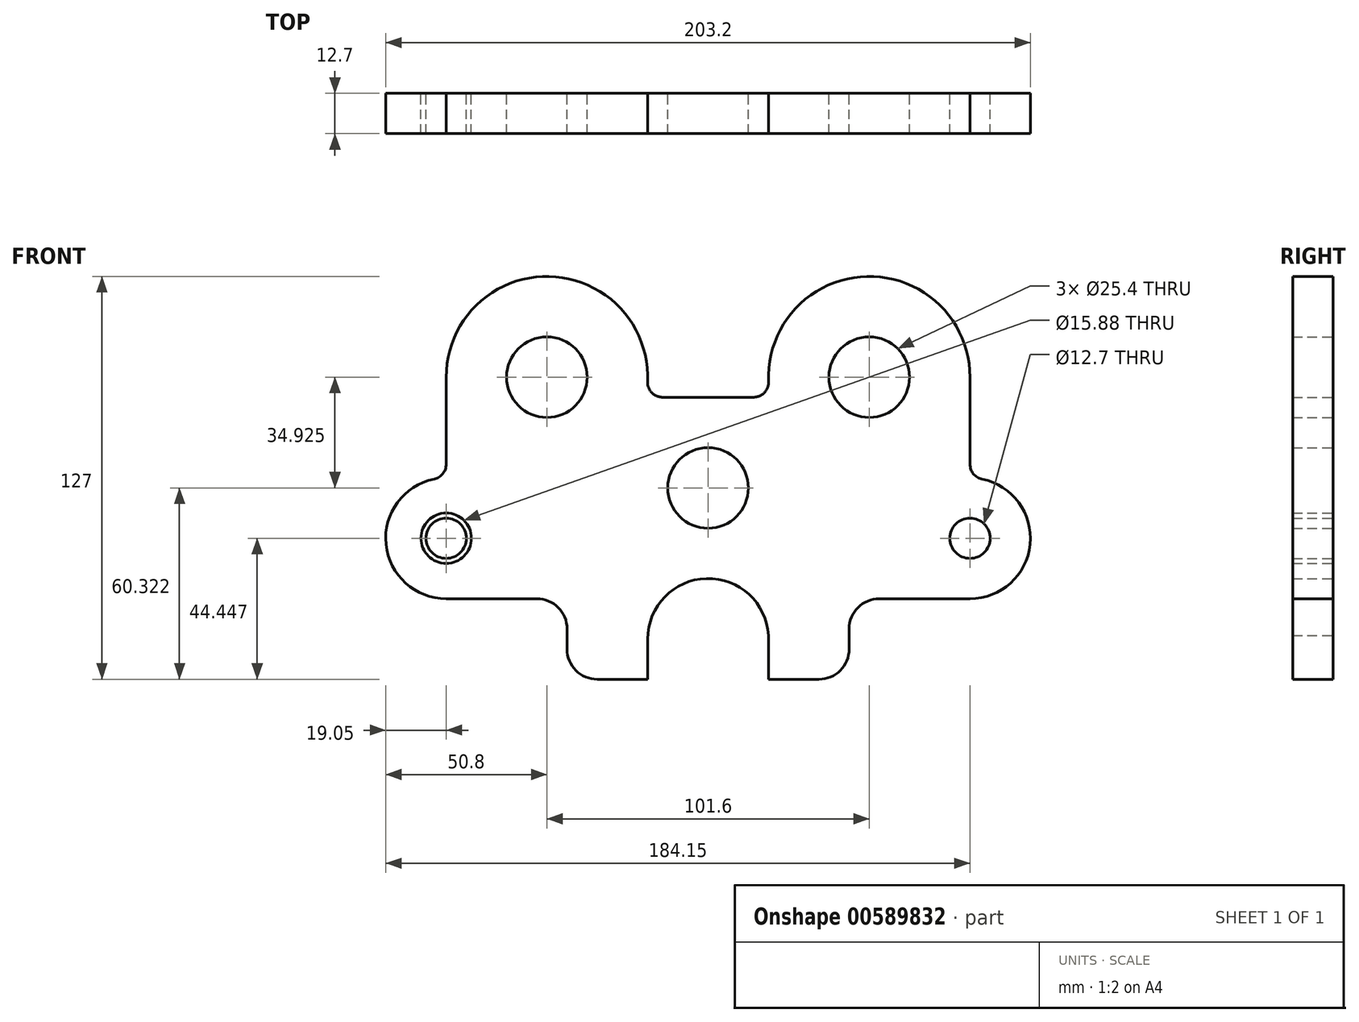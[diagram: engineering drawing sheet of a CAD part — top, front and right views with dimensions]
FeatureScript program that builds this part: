
annotation { "Feature Type Name" : "Feature", "Feature Type Description" : "" }
export const myFeature = defineFeature(function(context is Context, id is Id, definition is map)
    precondition{}
    {
        {
            var Q0;
            Q0=qCreatedBy(makeId("Front.planeOp"),FACE);
            var sketch = newSketch(context, id + "F0", { "sketchPlane" : qUnion([Q0])});
            skCircle(sketch, "E0", {"center": v(0, -42.39) * mm, "radius": 12.7 * mm});
            skCircle(sketch, "E1", {"center": v(50.8, -7.46) * mm, "radius": 12.7 * mm});
            skCircle(sketch, "E2", {"center": v(82.55, -58.26) * mm, "radius": 6.35 * mm});
            skCircle(sketch, "E3.MirrorC", {"center": v(-50.8, -7.46) * mm, "radius": 12.7 * mm});
            skCircle(sketch, "E4.MirrorC", {"center": v(-82.55, -58.26) * mm, "radius": 6.35 * mm});
            skArc(sketch, "E5", {"start": v(19.08, -8.84) * mm, "mid": v(50.1, 24.28) * mm, "end": v(82.55, -7.46) * mm});
            skArc(sketch, "E6", {"start": v(-19.08, -8.84) * mm, "mid": v(-50.1, 24.28) * mm, "end": v(-82.55, -7.46) * mm});
            skArc(sketch, "E7", {"start": v(-86.36, -39.6) * mm, "mid": v(-101.5, -60.18) * mm, "end": v(-82.55, -77.31) * mm});
            skArc(sketch, "E8", {"start": v(86.36, -39.6) * mm, "mid": v(101.5, -60.18) * mm, "end": v(82.55, -77.31) * mm});
            skLineSegment(sketch, "E9", {"start": v(82.55, -7.46) * mm, "end": v(82.55, -34.93) * mm});
            skLineSegment(sketch, "E10.MirrorCS", {"start": v(-82.55, -7.46) * mm, "end": v(-82.55, -34.93) * mm});
            skLineSegment(sketch, "E11", {"start": v(0, 87.14) * mm, "end": v(0, -112.55) * mm, "construction": true});
            skLineSegment(sketch, "E12", {"start": v(-82.55, -77.31) * mm, "end": v(-53.97, -77.31) * mm});
            skLineSegment(sketch, "E13", {"start": v(-44.45, -86.84) * mm, "end": v(-44.45, -93.19) * mm});
            skLineSegment(sketch, "E14", {"start": v(-34.92, -102.71) * mm, "end": v(-19.03, -102.71) * mm});
            skLineSegment(sketch, "E15.MirrorCS", {"start": v(82.55, -77.31) * mm, "end": v(53.98, -77.31) * mm});
            skLineSegment(sketch, "E16.MirrorCS", {"start": v(44.45, -86.84) * mm, "end": v(44.45, -93.19) * mm});
            skLineSegment(sketch, "E17.MirrorCS", {"start": v(34.93, -102.71) * mm, "end": v(19.03, -102.71) * mm});
            skLineSegment(sketch, "E18", {"start": v(-19.03, -102.71) * mm, "end": v(-19.03, -90.01) * mm});
            skArc(sketch, "E19", {"start": v(-19.03, -90.01) * mm, "mid": v(-0.52, -70.97) * mm, "end": v(19.04, -88.94) * mm});
            skLineSegment(sketch, "E20", {"start": v(19.03, -102.71) * mm, "end": v(19.04, -88.94) * mm});
            skPoint(sketch, "E21.visualSharp", {"position": v(-82.55, -39.21) * mm});
            skArc(sketch, "E21.filletArc", {"start": v(-86.36, -39.6) * mm, "mid": v(-83.62, -37.94) * mm, "end": v(-82.55, -34.93) * mm});
            skPoint(sketch, "E22.visualSharp", {"position": v(-44.45, -77.31) * mm});
            skArc(sketch, "E22.filletArc", {"start": v(-44.45, -86.84) * mm, "mid": v(-47.24, -80.1) * mm, "end": v(-53.97, -77.31) * mm});
            skPoint(sketch, "E23.visualSharp", {"position": v(-44.45, -102.71) * mm});
            skArc(sketch, "E23.filletArc", {"start": v(-44.45, -93.19) * mm, "mid": v(-41.66, -99.92) * mm, "end": v(-34.92, -102.71) * mm});
            skPoint(sketch, "E24.visualSharp", {"position": v(82.55, -39.21) * mm});
            skArc(sketch, "E24.filletArc", {"start": v(82.55, -34.93) * mm, "mid": v(83.62, -37.94) * mm, "end": v(86.36, -39.6) * mm});
            skPoint(sketch, "E25.visualSharp", {"position": v(44.45, -77.31) * mm});
            skArc(sketch, "E25.filletArc", {"start": v(53.98, -77.31) * mm, "mid": v(47.24, -80.1) * mm, "end": v(44.45, -86.84) * mm});
            skPoint(sketch, "E26.visualSharp", {"position": v(44.45, -102.71) * mm});
            skArc(sketch, "E26.filletArc", {"start": v(34.93, -102.71) * mm, "mid": v(41.66, -99.92) * mm, "end": v(44.45, -93.19) * mm});
            skLineSegment(sketch, "E27", {"start": v(-14.32, -13.81) * mm, "end": v(0, -13.81) * mm});
            skLineSegment(sketch, "E28.MirrorCS", {"start": v(14.32, -13.81) * mm, "end": v(0, -13.81) * mm});
            skPoint(sketch, "E29.visualSharp", {"position": v(-19.74, -13.81) * mm});
            skArc(sketch, "E29.filletArc", {"start": v(-19.08, -8.84) * mm, "mid": v(-17.76, -12.34) * mm, "end": v(-14.32, -13.81) * mm});
            skPoint(sketch, "E30.visualSharp", {"position": v(19.74, -13.81) * mm});
            skArc(sketch, "E30.filletArc", {"start": v(14.32, -13.81) * mm, "mid": v(17.76, -12.34) * mm, "end": v(19.08, -8.84) * mm});
            skCircle(sketch, "E31", {"center": v(-82.55, -58.26) * mm, "radius": 7.94 * mm});
            skCircle(sketch, "E32", {"center": v(82.55, -58.26) * mm, "radius": 7.94 * mm});
            skSolve(sketch);
        }
        {
            var Q0;
            Q0=makeQuery(id+"F0.imprint","IMPRINT",FACE,{"disambiguationData":[TD([[makeQuery(id+"F0.imprint","IMPRINT",EDGE,{"derivedFrom":sQuery(id+"F0.wireOp",EDGE,"E0")}),-1.0]])]});
            var Q1;
            Q1=makeQuery(id+"F0.imprint","IMPRINT",FACE,{"disambiguationData":[TD([[makeQuery(id+"F0.imprint","IMPRINT",EDGE,{"derivedFrom":sQuery(id+"F0.wireOp",EDGE,"E2")}),-1.0]])]});
            var Q2;
            Q2=makeQuery(id+"F0.imprint","IMPRINT",FACE,{"disambiguationData":[TD([[makeQuery(id+"F0.imprint","IMPRINT",EDGE,{"derivedFrom":sQuery(id+"F0.wireOp",EDGE,"E4.MirrorC")}),1.0]])]});
            extrude(context, id + "F1", {"entities" : qUnion([Q0, Q1, Q2]), "endBound" : BoundingType.SYMMETRIC, "depth" : 12.7 * mm, "offsetDistance" : 25.4 * mm});
        }
    });
